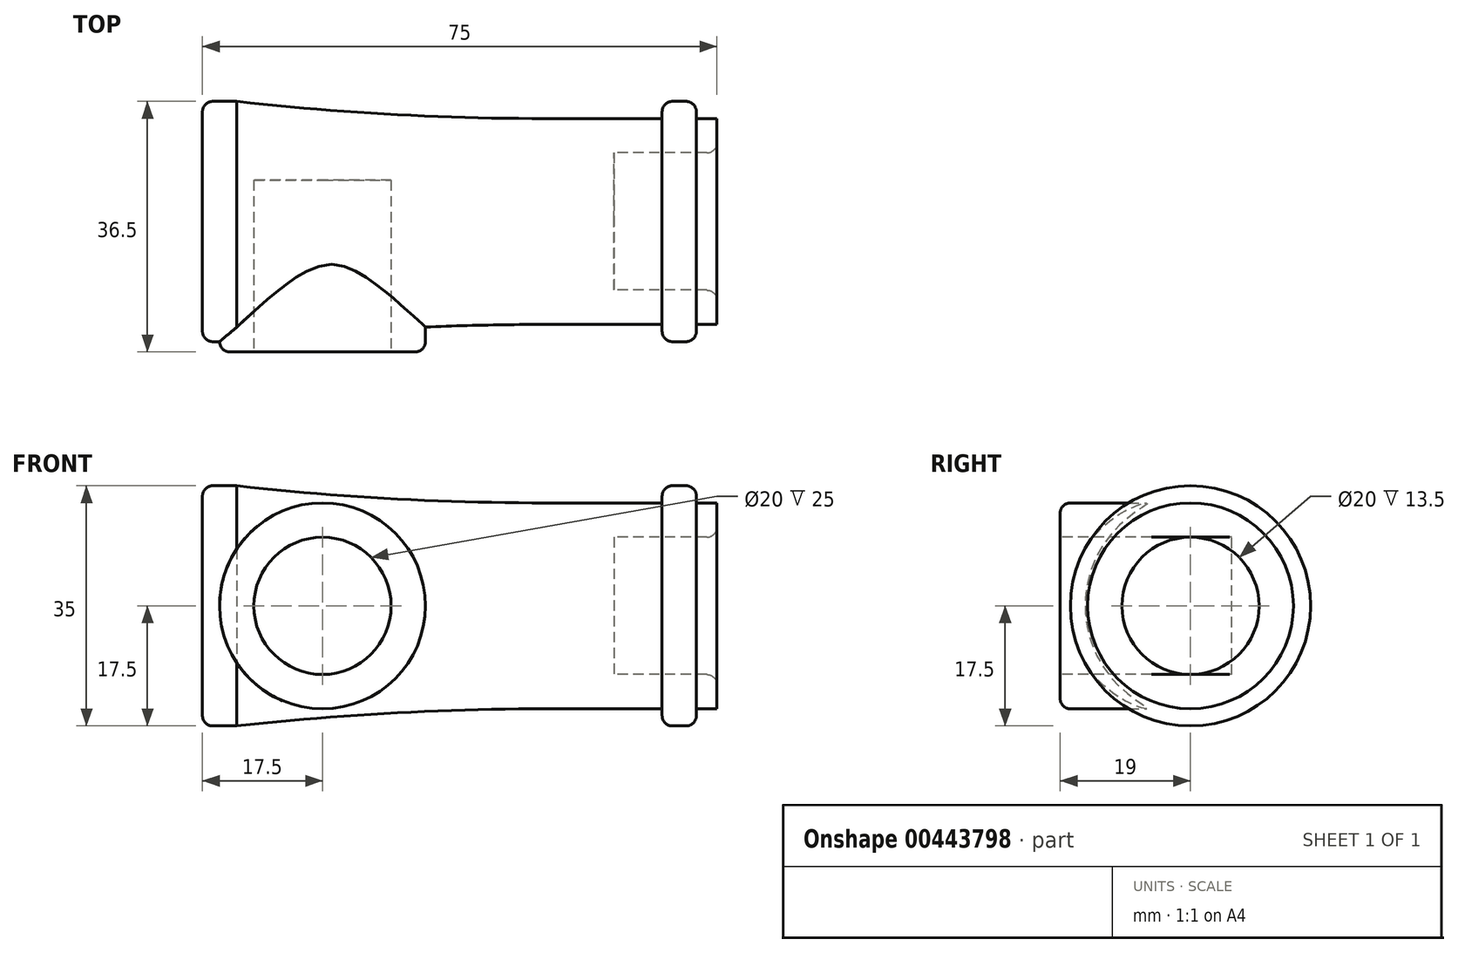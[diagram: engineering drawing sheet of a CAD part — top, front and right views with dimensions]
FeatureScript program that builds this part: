
annotation { "Feature Type Name" : "Feature", "Feature Type Description" : "" }
export const myFeature = defineFeature(function(context is Context, id is Id, definition is map)
    precondition{}
    {
        {
            var Q0;
            Q0=qCreatedBy(makeId("Front.planeOp"),FACE);
            var sketch = newSketch(context, id + "F0", { "sketchPlane" : qUnion([Q0])});
            skLineSegment(sketch, "E0", {"start": v(0, 0) * mm, "end": v(0, 17.5) * mm});
            skLineSegment(sketch, "E1", {"start": v(0, 17.5) * mm, "end": v(5, 17.5) * mm});
            skLineSegment(sketch, "E2", {"start": v(0, 0) * mm, "end": v(60, 0) * mm});
            skLineSegment(sketch, "E3", {"start": v(60, 0) * mm, "end": v(60, 10) * mm});
            skLineSegment(sketch, "E4", {"start": v(60, 10) * mm, "end": v(75, 10) * mm});
            skLineSegment(sketch, "E5", {"start": v(75, 10) * mm, "end": v(75, 15) * mm});
            skLineSegment(sketch, "E6", {"start": v(75, 15) * mm, "end": v(72, 15) * mm});
            skLineSegment(sketch, "E7", {"start": v(72, 15) * mm, "end": v(72, 17.5) * mm});
            skLineSegment(sketch, "E8", {"start": v(72, 17.5) * mm, "end": v(67, 17.5) * mm});
            skLineSegment(sketch, "E9", {"start": v(67, 17.5) * mm, "end": v(67, 15) * mm});
            skLineSegment(sketch, "E10", {"start": v(67, 15) * mm, "end": v(50, 15) * mm});
            skArc(sketch, "E11", {"start": v(5, 17.5) * mm, "mid": v(27.47, 15.63) * mm, "end": v(50, 15) * mm});
            skSolve(sketch);
        }
        {
            var Q0;
            Q0=makeQuery(id+"F0.imprint","IMPRINT",FACE,{"disambiguationData":[TD([[makeQuery(id+"F0.imprint","IMPRINT",EDGE,{"derivedFrom":sQuery(id+"F0.wireOp",EDGE,"E0")}),-1.0]])]});
            var Q1;
            Q1=sQuery(id+"F0.wireOp",EDGE,"E2");
            revolve(context, id + "F1", {"entities" : qUnion([Q0]), "axis" : qUnion([Q1]), "revolveType" : RevolveType.FULL});
        }
        {
            var Q0;
            Q0=qCreatedBy(makeId("Front.planeOp"),FACE);
            var sketch = newSketch(context, id + "F2", { "sketchPlane" : qUnion([Q0])});
            skCircle(sketch, "E12", {"center": v(17.5, 0) * mm, "radius": 15 * mm});
            skSolve(sketch);
        }
        {
            var Q0;
            Q0 = qSketchRegion(id + "F2", true);
            extrude(context, id + "F3", {"entities" : qUnion([Q0]), "operationType" : NewBodyOperationType.ADD, "depth" : 19 * mm});
        }
        {
            var Q0;
            Q0=makeQuery(id+"F3.opExtrude","CAP_FACE",FACE,{"disambiguationData":[OSD([sQuery(id+"F2.wireOp",EDGE,"E12")])],"isStart":false});
            var sketch = newSketch(context, id + "F4", { "sketchPlane" : qUnion([Q0])});
            skCircle(sketch, "E13", {"center": v(17.5, 0) * mm, "radius": 10 * mm});
            skSolve(sketch);
        }
        {
            var Q0;
            Q0 = qSketchRegion(id + "F4", true);
            extrude(context, id + "F5", {"entities" : qUnion([Q0]), "operationType" : NewBodyOperationType.REMOVE, "oppositeDirection" : true, "depth" : 25 * mm});
        }
        {
            var Q0;
            Q0=makeQuery(id+"F1.opRevolve","SWEPT_EDGE",EDGE,{"disambiguationData":[OSD([sQuery(id+"F0.wireOp",EDGE,"E0"),sQuery(id+"F0.wireOp",EDGE,"E1")])]});
            var Q1;
            Q1=makeQuery(id+"F3.opExtrude","CAP_EDGE",EDGE,{"disambiguationData":[OSD([sQuery(id+"F2.wireOp",EDGE,"E12")])],"isStart":false});
            fillet(context, id + "F6", {"entities" : qUnion([Q0, Q1]), "radius" : 1.5 * mm, "tangentPropagation" : true, "allowEdgeOverflow" : false});
        }
        {
            var Q0;
            Q0=makeQuery(id+"F1.opRevolve","SWEPT_EDGE",EDGE,{"disambiguationData":[OSD([sQuery(id+"F0.wireOp",EDGE,"E8"),sQuery(id+"F0.wireOp",EDGE,"E9")])]});
            var Q1;
            Q1=makeQuery(id+"F1.opRevolve","SWEPT_EDGE",EDGE,{"disambiguationData":[OSD([sQuery(id+"F0.wireOp",EDGE,"E7"),sQuery(id+"F0.wireOp",EDGE,"E8")])]});
            var Q2;
            Q2=makeQuery(id+"F1.opRevolve","SWEPT_EDGE",EDGE,{"disambiguationData":[OSD([sQuery(id+"F0.wireOp",EDGE,"E4"),sQuery(id+"F0.wireOp",EDGE,"E5")])]});
            fillet(context, id + "F7", {"entities" : qUnion([Q0, Q1, Q2]), "radius" : 1.5 * mm, "tangentPropagation" : true, "allowEdgeOverflow" : false});
        }
    });
